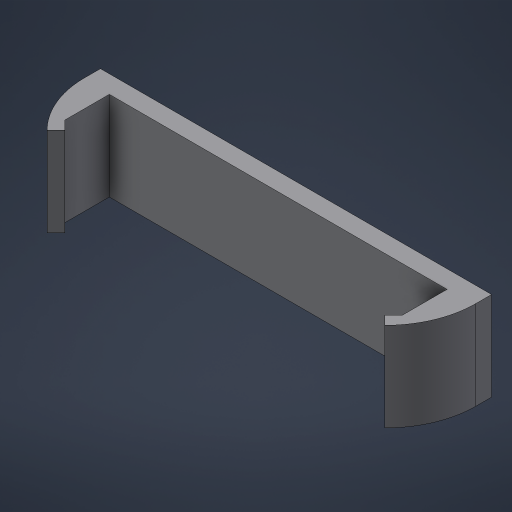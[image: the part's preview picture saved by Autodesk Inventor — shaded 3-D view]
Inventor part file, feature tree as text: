
AUTODESK INVENTOR PART (.ipt)
format: ipt  version: 2023.5 (Build 275446000, 446)  size: 391,680 bytes
history: native  units: mm
features: extrude x1, mirror x1, sketch x1
ambient origin geometry x8: Origin, YZ Plane, XZ Plane, XY Plane, X Axis, Y Axis, Z Axis, Center Point
bodies: Volumenkörper1 (feature_tree)
feature tree (3):
  extrude  "Extrusion1"  Depth=10.0mm
  mirror  "Spiegeln1"
  sketch  "Skizze1"  dims[d6=19.0mm d7=5.0mm d8=3.0mm d9=1.0mm d10=2.0mm d11=2.0mm d12=10.0mm d13=0.0mm]
